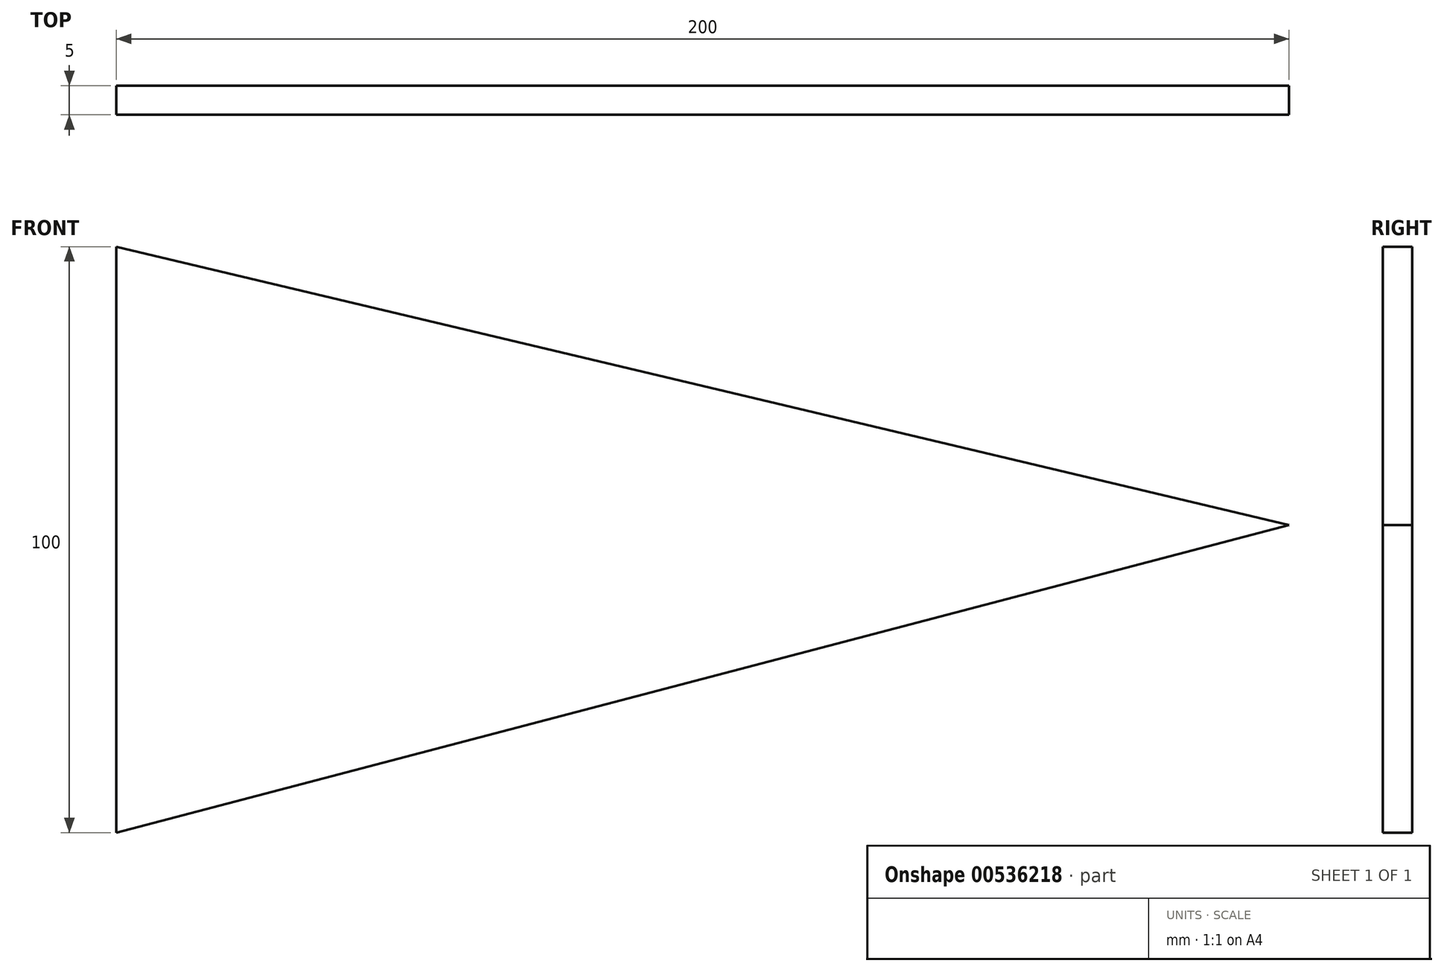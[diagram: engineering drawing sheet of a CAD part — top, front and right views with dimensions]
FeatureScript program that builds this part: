
annotation { "Feature Type Name" : "Feature", "Feature Type Description" : "" }
export const myFeature = defineFeature(function(context is Context, id is Id, definition is map)
    precondition{}
    {
        {
            var Q0;
            Q0=qCreatedBy(makeId("Front.planeOp"),FACE);
            var sketch = newSketch(context, id + "F0", { "sketchPlane" : qUnion([Q0])});
            skLineSegment(sketch, "E0", {"start": v(-60.64, -44.5) * mm, "end": v(139.36, 8) * mm});
            skLineSegment(sketch, "E1", {"start": v(-60.64, 55.5) * mm, "end": v(139.36, 8) * mm});
            skLineSegment(sketch, "E2", {"start": v(-60.64, 55.5) * mm, "end": v(-60.64, -44.5) * mm});
            skSolve(sketch);
        }
        {
            var Q0;
            Q0=makeQuery(id+"F0.imprint","IMPRINT",FACE,{"disambiguationData":[TD([[makeQuery(id+"F0.imprint","IMPRINT",EDGE,{"derivedFrom":sQuery(id+"F0.wireOp",EDGE,"E0")}),1.0]])]});
            extrude(context, id + "F1", {"entities" : qUnion([Q0]), "depth" : 5 * mm, "offsetDistance" : 25 * mm});
        }
    });
